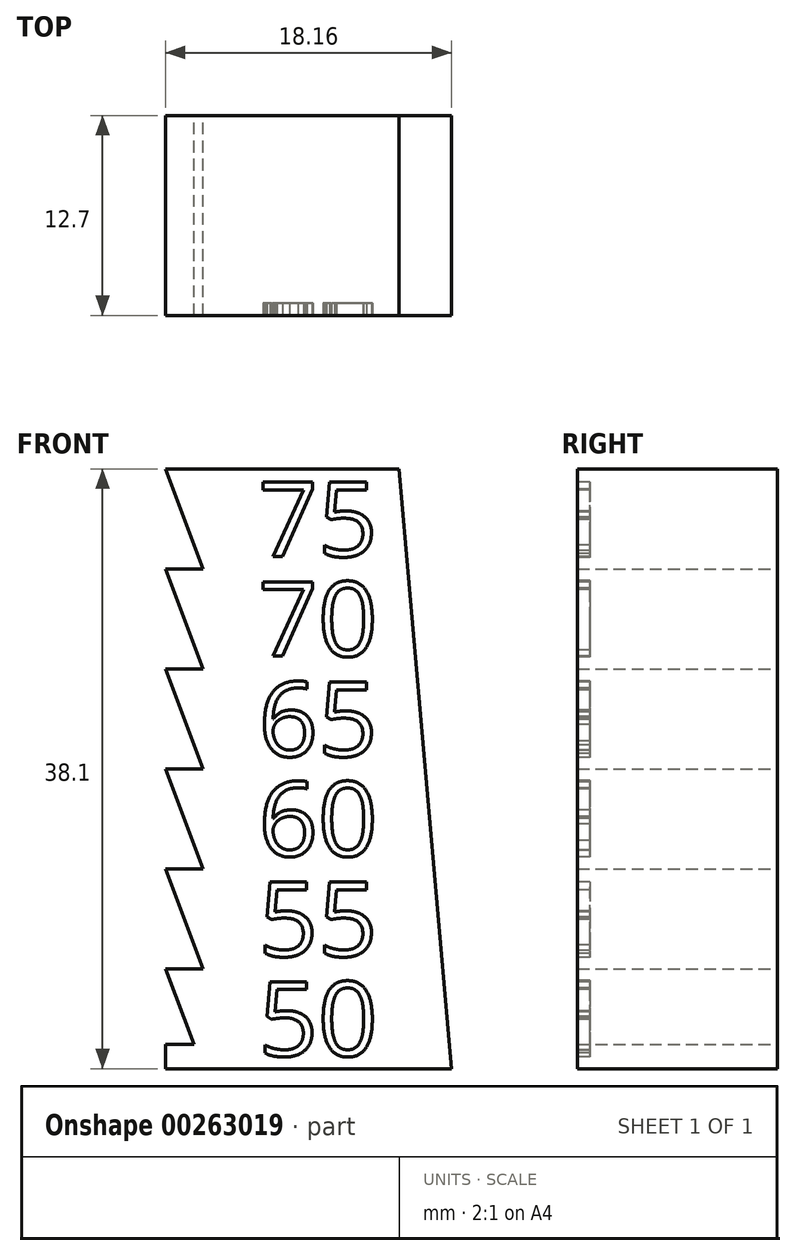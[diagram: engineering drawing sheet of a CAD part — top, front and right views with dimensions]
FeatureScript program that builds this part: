
annotation { "Feature Type Name" : "Feature", "Feature Type Description" : "" }
export const myFeature = defineFeature(function(context is Context, id is Id, definition is map)
    precondition{}
    {
        {
            var Q0;
            Q0=qCreatedBy(makeId("Front.planeOp"),FACE);
            var sketch = newSketch(context, id + "F0", { "sketchPlane" : qUnion([Q0])});
            skLineSegment(sketch, "E0", {"start": v(2.13, 38.1) * mm, "end": v(-12.7, 38.1) * mm});
            skLineSegment(sketch, "E1.0", {"start": v(-12.7, 6.35) * mm, "end": v(-10.3, 6.35) * mm});
            skLineSegment(sketch, "E2.0", {"start": v(-12.7, 12.7) * mm, "end": v(-10.3, 12.7) * mm});
            skLineSegment(sketch, "E3.0", {"start": v(-12.7, 19.05) * mm, "end": v(-10.3, 19.05) * mm});
            skLineSegment(sketch, "E4.0", {"start": v(-12.7, 25.4) * mm, "end": v(-10.3, 25.4) * mm});
            skLineSegment(sketch, "E5.0", {"start": v(-12.7, 31.75) * mm, "end": v(-10.3, 31.75) * mm});
            skLineSegment(sketch, "E6", {"start": v(-12.7, 6.35) * mm, "end": v(-10.9, 1.56) * mm});
            skLineSegment(sketch, "E7.0", {"start": v(-12.7, 1.56) * mm, "end": v(-10.9, 1.56) * mm});
            skLineSegment(sketch, "E8.trimOffspring", {"start": v(-12.7, 1.56) * mm, "end": v(-12.7, 0) * mm});
            skLineSegment(sketch, "E9.0.2.0", {"start": v(-12.7, 19.05) * mm, "end": v(-10.3, 12.7) * mm});
            skLineSegment(sketch, "E9.0.3.0", {"start": v(-12.7, 25.4) * mm, "end": v(-10.3, 19.05) * mm});
            skLineSegment(sketch, "E9.0.4.0", {"start": v(-12.7, 31.75) * mm, "end": v(-10.3, 25.4) * mm});
            skLineSegment(sketch, "E9.direction1", {"start": v(-10.9, 1.56) * mm, "end": v(14.5, 1.56) * mm, "construction": true});
            skLineSegment(sketch, "E10.0.0.5", {"start": v(-12.7, 38.1) * mm, "end": v(-10.3, 31.75) * mm});
            skLineSegment(sketch, "E11", {"start": v(-10.3, 6.35) * mm, "end": v(-12.7, 12.7) * mm});
            skLineSegment(sketch, "E12", {"start": v(-12.7, 0) * mm, "end": v(5.46, 0) * mm});
            skLineSegment(sketch, "E13", {"start": v(5.46, 0) * mm, "end": v(2.13, 38.1) * mm});
            skSolve(sketch);
        }
        {
            var Q0;
            Q0=makeQuery(id+"F0.imprint","IMPRINT",FACE,{"disambiguationData":[TD([[makeQuery(id+"F0.imprint","IMPRINT",EDGE,{"derivedFrom":sQuery(id+"F0.wireOp",EDGE,"E0")}),1.0]])]});
            extrude(context, id + "F1", {"entities" : qUnion([Q0]), "depth" : 12.7 * mm});
        }
        {
            var Q0;
            Q0=makeQuery(id+"F1.opExtrude","CAP_FACE",FACE,{"disambiguationData":[OSD([sQuery(id+"F0.wireOp",EDGE,"E0"),sQuery(id+"F0.wireOp",EDGE,"E1.0"),sQuery(id+"F0.wireOp",EDGE,"E2.0"),sQuery(id+"F0.wireOp",EDGE,"E3.0"),sQuery(id+"F0.wireOp",EDGE,"E4.0"),sQuery(id+"F0.wireOp",EDGE,"E5.0"),sQuery(id+"F0.wireOp",EDGE,"E6"),sQuery(id+"F0.wireOp",EDGE,"E7.0"),sQuery(id+"F0.wireOp",EDGE,"E8.trimOffspring"),sQuery(id+"F0.wireOp",EDGE,"E9.0.2.0"),sQuery(id+"F0.wireOp",EDGE,"E9.0.3.0"),sQuery(id+"F0.wireOp",EDGE,"E9.0.4.0"),sQuery(id+"F0.wireOp",EDGE,"E10.0.0.5"),sQuery(id+"F0.wireOp",EDGE,"E11"),sQuery(id+"F0.wireOp",EDGE,"AnPRvBk4-Mrcv-P1cr-40so-xAUHJ6QT8sw4"),sQuery(id+"F0.wireOp",EDGE,"E12")])],"isStart":false});
            var sketch = newSketch(context, id + "F2", { "sketchPlane" : qUnion([Q0])});
            skLineSegment(sketch, "E14", {"start": v(-3.62, 0) * mm, "end": v(-3.62, 0.8) * mm, "construction": true});
            skLineSegment(sketch, "E15", {"start": v(-3.62, 0.8) * mm, "end": v(-6.8, 0.8) * mm, "construction": true});
            skLineSegment(sketch, "E16", {"start": v(-6.8, 0.8) * mm, "end": v(-6.8, 5.56) * mm, "construction": true});
            skLineSegment(sketch, "E17", {"start": v(-6.8, 5.56) * mm, "end": v(0.87, 5.56) * mm, "construction": true});
            skLineSegment(sketch, "E18.0.1.0", {"start": v(-6.8, 7.14) * mm, "end": v(-6.8, 11.9) * mm, "construction": true});
            skLineSegment(sketch, "E18.0.1.1", {"start": v(-3.62, 7.14) * mm, "end": v(-6.8, 7.14) * mm, "construction": true});
            skLineSegment(sketch, "E18.0.1.2", {"start": v(-6.8, 11.9) * mm, "end": v(0.82, 11.9) * mm, "construction": true});
            skLineSegment(sketch, "E18.0.2.0", {"start": v(-6.8, 13.5) * mm, "end": v(-6.8, 18.26) * mm, "construction": true});
            skLineSegment(sketch, "E18.0.2.1", {"start": v(-3.62, 13.5) * mm, "end": v(-6.8, 13.5) * mm, "construction": true});
            skLineSegment(sketch, "E18.0.2.2", {"start": v(-6.8, 18.26) * mm, "end": v(0.87, 18.26) * mm, "construction": true});
            skLineSegment(sketch, "E18.0.3.0", {"start": v(-6.8, 19.84) * mm, "end": v(-6.8, 24.6) * mm, "construction": true});
            skLineSegment(sketch, "E18.0.3.1", {"start": v(-3.62, 19.84) * mm, "end": v(-6.8, 19.84) * mm, "construction": true});
            skLineSegment(sketch, "E18.0.3.2", {"start": v(-6.8, 24.6) * mm, "end": v(0.82, 24.6) * mm, "construction": true});
            skLineSegment(sketch, "E18.0.4.0", {"start": v(-6.8, 26.2) * mm, "end": v(-6.8, 30.96) * mm, "construction": true});
            skLineSegment(sketch, "E18.0.4.1", {"start": v(-3.62, 26.2) * mm, "end": v(-6.8, 26.2) * mm, "construction": true});
            skLineSegment(sketch, "E18.0.4.2", {"start": v(-6.8, 30.96) * mm, "end": v(0.87, 30.96) * mm, "construction": true});
            skLineSegment(sketch, "E18.0.5.0", {"start": v(-6.8, 32.54) * mm, "end": v(-6.8, 37.3) * mm, "construction": true});
            skLineSegment(sketch, "E18.0.5.1", {"start": v(-3.62, 32.54) * mm, "end": v(-6.8, 32.54) * mm, "construction": true});
            skLineSegment(sketch, "E18.0.5.2", {"start": v(-6.8, 37.3) * mm, "end": v(0.82, 37.3) * mm, "construction": true});
            skText(sketch, "E19", { "text": "50", "fontName": "OpenSans-Regular.ttf"});
            skText(sketch, "E20", { "text": "55", "fontName": "OpenSans-Regular.ttf"});
            skText(sketch, "E21", { "text": "60", "fontName": "OpenSans-Regular.ttf"});
            skText(sketch, "E22", { "text": "65", "fontName": "OpenSans-Regular.ttf"});
            skText(sketch, "E23", { "text": "70", "fontName": "OpenSans-Regular.ttf"});
            skText(sketch, "E24", { "text": "75", "fontName": "OpenSans-Regular.ttf"});
            const initialGuessF2  = {"E19": [-0.0068, 0.0008, 1, 0, 0.00476], "E20": [-0.0068, 0.00714, 1, 0, 0.00476], "E21": [-0.0068, 0.0135, 1, 0, 0.00476], "E22": [-0.0068, 0.01984, 1, 0, 0.00476], "E23": [-0.0068, 0.0262, 1, 0, 0.00476], "E24": [-0.0068, 0.03254, 1, 0, 0.00476]};
            skSetInitialGuess(sketch, initialGuessF2);
            skSolve(sketch);
        }
        {
            var Q0;
            Q0=makeQuery(id+"F2.imprint","IMPRINT",FACE,{"disambiguationData":[TD([[makeQuery(id+"F2.imprint","IMPRINT",EDGE,{"derivedFrom":sQuery(id+"F2.wireOp",EDGE,"E24.sketch_text.stroke-0")}),-1.0]])]});
            var Q1;
            Q1=makeQuery(id+"F2.imprint","IMPRINT",FACE,{"disambiguationData":[TD([[makeQuery(id+"F2.imprint","IMPRINT",EDGE,{"derivedFrom":sQuery(id+"F2.wireOp",EDGE,"E24.sketch_text.stroke-7")}),-1.0]])]});
            var Q2;
            Q2=makeQuery(id+"F2.imprint","IMPRINT",FACE,{"disambiguationData":[TD([[makeQuery(id+"F2.imprint","IMPRINT",EDGE,{"derivedFrom":sQuery(id+"F2.wireOp",EDGE,"E23.sketch_text.stroke-0")}),-1.0]])]});
            var Q3;
            Q3=makeQuery(id+"F2.imprint","IMPRINT",FACE,{"disambiguationData":[TD([[makeQuery(id+"F2.imprint","IMPRINT",EDGE,{"derivedFrom":sQuery(id+"F2.wireOp",EDGE,"E23.sketch_text.stroke-7")}),-1.0]])]});
            var Q4;
            Q4=makeQuery(id+"F2.imprint","IMPRINT",FACE,{"disambiguationData":[TD([[makeQuery(id+"F2.imprint","IMPRINT",EDGE,{"derivedFrom":sQuery(id+"F2.wireOp",EDGE,"E22.sketch_text.stroke-0")}),-1.0]])]});
            var Q5;
            Q5=makeQuery(id+"F2.imprint","IMPRINT",FACE,{"disambiguationData":[TD([[makeQuery(id+"F2.imprint","IMPRINT",EDGE,{"derivedFrom":sQuery(id+"F2.wireOp",EDGE,"E22.sketch_text.stroke-25")}),-1.0]])]});
            var Q6;
            Q6=makeQuery(id+"F2.imprint","IMPRINT",FACE,{"disambiguationData":[TD([[makeQuery(id+"F2.imprint","IMPRINT",EDGE,{"derivedFrom":sQuery(id+"F2.wireOp",EDGE,"E21.sketch_text.stroke-0")}),-1.0]])]});
            var Q7;
            Q7=makeQuery(id+"F2.imprint","IMPRINT",FACE,{"disambiguationData":[TD([[makeQuery(id+"F2.imprint","IMPRINT",EDGE,{"derivedFrom":sQuery(id+"F2.wireOp",EDGE,"E21.sketch_text.stroke-25")}),-1.0]])]});
            var Q8;
            Q8=makeQuery(id+"F2.imprint","IMPRINT",FACE,{"disambiguationData":[TD([[makeQuery(id+"F2.imprint","IMPRINT",EDGE,{"derivedFrom":sQuery(id+"F2.wireOp",EDGE,"E20.sketch_text.stroke-0")}),-1.0]])]});
            var Q9;
            Q9=makeQuery(id+"F2.imprint","IMPRINT",FACE,{"disambiguationData":[TD([[makeQuery(id+"F2.imprint","IMPRINT",EDGE,{"derivedFrom":sQuery(id+"F2.wireOp",EDGE,"E20.sketch_text.stroke-19")}),-1.0]])]});
            var Q10;
            Q10=makeQuery(id+"F2.imprint","IMPRINT",FACE,{"disambiguationData":[TD([[makeQuery(id+"F2.imprint","IMPRINT",EDGE,{"derivedFrom":sQuery(id+"F2.wireOp",EDGE,"E19.sketch_text.stroke-0")}),-1.0]])]});
            var Q11;
            Q11=makeQuery(id+"F2.imprint","IMPRINT",FACE,{"disambiguationData":[TD([[makeQuery(id+"F2.imprint","IMPRINT",EDGE,{"derivedFrom":sQuery(id+"F2.wireOp",EDGE,"E19.sketch_text.stroke-19")}),-1.0]])]});
            extrude(context, id + "F3", {"entities" : qUnion([Q0, Q1, Q2, Q3, Q4, Q5, Q6, Q7, Q8, Q9, Q10, Q11]), "operationType" : NewBodyOperationType.REMOVE, "oppositeDirection" : true, "depth" : 0.8 * mm});
        }
    });
